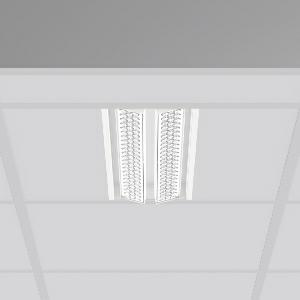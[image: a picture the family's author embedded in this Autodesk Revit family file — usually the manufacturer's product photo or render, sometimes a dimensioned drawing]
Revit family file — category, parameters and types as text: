
# Revit family: tx-move_901732_002_31d8
name_source: partatom
category: Lighting Fixtures
units: mm (PartAtom-declared; Revit-internal decimal feet)

## family parameters
Cut with Voids When Loaded = No
Host = Face
Light Source = No
Part Type = Normal
Room Calculation Point = No
Round Connector Dimension = Use Diameter
Shared = No

## types (1)
- MultiLumen 1 (1 x LED Modul 830, 2750 lm, 3000)
    Apparent Load = 35 VA
    Approval mark = CE
    CIE Flux Codes = 90 97 99 100 100
    Color Rendering = 80
    Color Temperature = 3000
    Default Elevation = 1800 mm
    Description = Series: TX-MOVE
Einlege/Einbau-Flächenstrahler. Housing: sheet steel, powder-coated. 2xSwivel range: 90°. High-efficiency LED units with optimum light control thanks to clear plastic (PC) lens optics. Spezielle Mikrostrukturen reduzieren Gelbsaum. Symmetrical light distribution. Suitable for laying in grid ceiling module 600. Connected converter included in separate gearbox.Suitable for through-wiring.MultiLumen: Luminous flux adjustable in 3 steps. Accessories: Mounting frame for installation in suspended ceilings. Environmentally friendly and resource-saving due to replaceable and recyclable components. 
Colour: traffic white, matt (RAL 9016)
Length: 597 mm
Width: 190 mm
Height: 39 mm
Cut-out length: 577.5 mm
Cut-out width: 174 mm
Recess height: 100 mm
Lamp: LED
Socket: without socket
Colour temperature: 3000K
Colour rendering index (CRI): 80
System power: 35 W
Rated luminous flux: 5500 lm
Luminous efficiency: 157 lm/W
System power 2: 47 W
Rated luminous flux 2: 7100 lm
Luminous efficiency 2: 151 lm/W
System power 3: 68 W
Rated luminous flux 3: 9700 lm
Luminous efficiency 3: 143 lm/W
Control gear: Regulated power supply
Protection class: I
Type of protection: IP 20
    Height = 0 mm  [stored 0 ft]
    Lamp = 1 x LED Modul 830
    Lamp Light Flux = 2750 lm
    Lamp count = 1
    Length = 597 mm
    Lifetime = 50000 h
    Luminous efficacy = 157 lm/W
    Manufacturer = RZB
    ModVariant = No
    Model = 901732.002
    Mounting Place = Ceiling, Wall
    Mounting Type = Recessed
    Number of Poles = 1
    OnlyDefault = Yes
    Power Factor = 1
    Product Name = TX-MOVE
    Product group = Recessed projectors
    ProductGroupID = 401
    Protection Class = Protection class I
    Protection Degree = IP 20
    RLX_Detail_Level = 1
    RLX_Emergency_Light_Flux = 0 lm
    RLX_Emergency_Type = 0
    RLX_Emergency_Type_DB = No
    RlxData = <blob elided: 35377 chars, md5=6c05e490>
    Socket = socket
    Standby Power = 0 W
    System Light Flux = 5500 lm
    System Power = 35 W
    Type Comments = MultiLumen 1
    Type Image = 901733.002.jpg
    URL = http://relux.com
    VarID = multilumen_1
    Voltage = 230 V
    Voltage Range = 220-240 V
    Weight = 0.00 kg
    Width = 190 mm  [stored 0.62336 ft]

note: [stored X ft] marks values corroborated as IEEE doubles in the binary element streams (Revit-internal decimal feet)

## geometry (parser evidence)
native form markers: Blend x4, Sweep x13
no freeform markers — native parametric forms only
